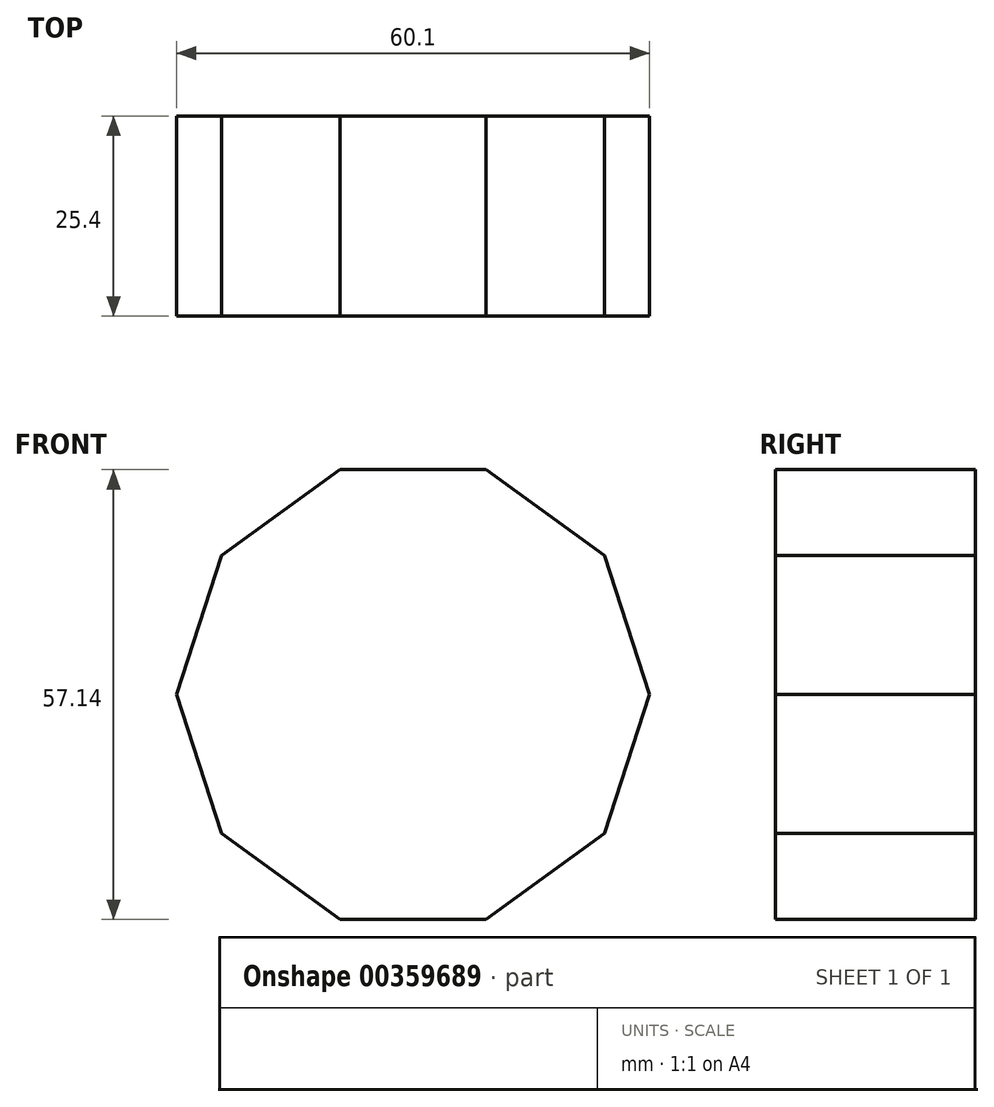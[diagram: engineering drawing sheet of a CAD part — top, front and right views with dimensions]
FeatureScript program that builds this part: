
annotation { "Feature Type Name" : "Feature", "Feature Type Description" : "" }
export const myFeature = defineFeature(function(context is Context, id is Id, definition is map)
    precondition{}
    {
        {
            var Q0;
            Q0=qCreatedBy(makeId("Front.planeOp"),FACE);
            var sketch = newSketch(context, id + "F0", { "sketchPlane" : qUnion([Q0])});
            skLineSegment(sketch, "E0", {"start": v(0, 0) * mm, "end": v(0, 28.58) * mm});
            skCircle(sketch, "E1.cCircle", {"center": v(0, 0) * mm, "radius": 28.58 * mm, "construction": true});
            skLineSegment(sketch, "E1.0", {"start": v(-9.28, 28.58) * mm, "end": v(9.28, 28.58) * mm});
            skLineSegment(sketch, "E1.1", {"start": v(9.28, 28.58) * mm, "end": v(24.3, 17.66) * mm});
            skLineSegment(sketch, "E1.2", {"start": v(24.3, 17.66) * mm, "end": v(30.05, 0) * mm});
            skLineSegment(sketch, "E1.3", {"start": v(30.05, 0) * mm, "end": v(24.3, -17.66) * mm});
            skLineSegment(sketch, "E1.4", {"start": v(24.3, -17.66) * mm, "end": v(9.28, -28.58) * mm});
            skLineSegment(sketch, "E1.5", {"start": v(9.28, -28.58) * mm, "end": v(-9.28, -28.58) * mm});
            skLineSegment(sketch, "E1.6", {"start": v(-9.28, -28.58) * mm, "end": v(-24.3, -17.66) * mm});
            skLineSegment(sketch, "E1.7", {"start": v(-24.3, -17.66) * mm, "end": v(-30.05, 0) * mm});
            skLineSegment(sketch, "E1.8", {"start": v(-30.05, 0) * mm, "end": v(-24.3, 17.66) * mm});
            skLineSegment(sketch, "E1.9", {"start": v(-24.3, 17.66) * mm, "end": v(-9.28, 28.58) * mm});
            skPoint(sketch, "E1.0.midPoint", {"position": v(0, 28.58) * mm});
            skSolve(sketch);
        }
        {
            var Q0;
            {var subQ3=sQuery(id+"F0.wireOp",EDGE,"E1.1");Q0=makeQuery(id+"F0.imprint","IMPRINT",FACE,{"disambiguationData":[TD([[makeQuery(id+"F0.imprint","IMPRINT",EDGE,{"derivedFrom":subQ3}),-1.0]])]});}
            extrude(context, id + "F1", {"entities" : qUnion([Q0]), "depth" : 25.4 * mm});
        }
    });
